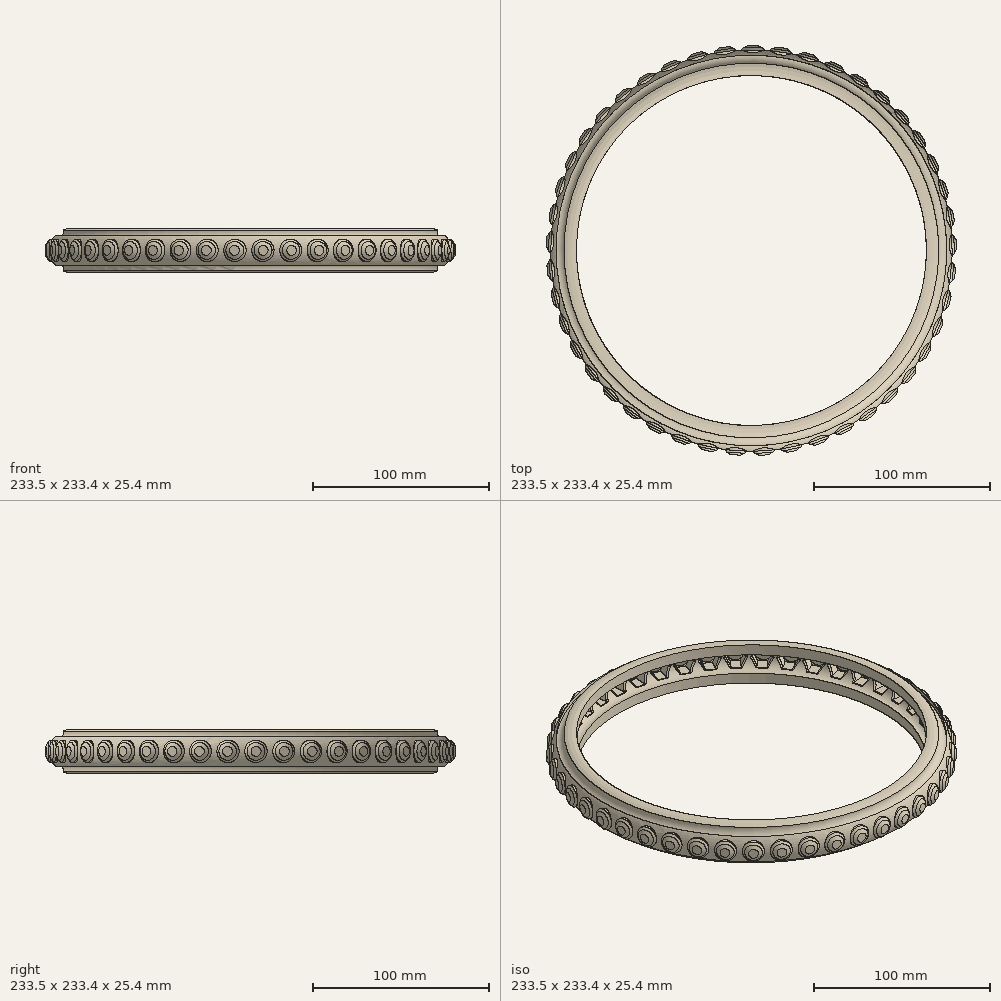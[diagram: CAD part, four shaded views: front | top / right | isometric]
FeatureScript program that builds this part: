
annotation { "Feature Type Name" : "Feature", "Feature Type Description" : "" }
export const myFeature = defineFeature(function(context is Context, id is Id, definition is map)
    precondition{}
    {
        {
            var Q0;
            Q0=qCreatedBy(makeId("Right.planeOp"),FACE);
            var sketch = newSketch(context, id + "F0", { "sketchPlane" : qUnion([Q0])});
            skCircle(sketch, "E0", {"center": v(101.6, 0) * mm, "radius": 6.35 * mm});
            skSolve(sketch);
        }
        {
            var Q0;
            Q0=qCreatedBy(makeId("Right.planeOp"),FACE);
            var sketch = newSketch(context, id + "F1", { "sketchPlane" : qUnion([Q0])});
            skLineSegment(sketch, "E1", {"start": v(0, 25.2) * mm, "end": v(0, -19.53) * mm, "construction": true});
            skSolve(sketch);
        }
        {
            var Q0;
            Q0 = qSketchRegion(id + "F0", true);
            var Q1;
            Q1=sQuery(id+"F1.wireOp",EDGE,"E1");
            revolve(context, id + "F2", {"entities" : qUnion([Q0]), "axis" : qUnion([Q1]), "revolveType" : RevolveType.FULL});
        }
        {
            var Q0;
            Q0=qCreatedBy(makeId("Top.planeOp"),FACE);
            var sketch = newSketch(context, id + "F3", { "sketchPlane" : qUnion([Q0])});
            skCircle(sketch, "E2", {"center": v(0, 0) * mm, "radius": 99.66 * mm});
            skSolve(sketch);
        }
        {
            var Q0;
            Q0=makeQuery(id+"F3.imprint","IMPRINT",FACE,{"disambiguationData":[TD([[makeQuery(id+"F3.imprint","IMPRINT",EDGE,{"derivedFrom":sQuery(id+"F3.wireOp",EDGE,"E2")}),1.0]])]});
            extrude(context, id + "F4", {"entities" : qUnion([Q0]), "operationType" : NewBodyOperationType.REMOVE, "endBound" : BoundingType.THROUGH_ALL, "depth" : 25.4 * mm, "hasSecondDirection" : true, "secondDirectionBound" : SecondDirectionBoundingType.THROUGH_ALL, "secondDirectionOppositeDirection" : true, "secondDirectionDepth" : 25.4 * mm});
        }
        {
            var Q0;
            Q0=makeQuery(id+"F4.boolean.opBoolean","COPY",FACE,{"derivedFrom":makeQuery(id+"F4.opExtrude","SWEPT_FACE",FACE,{"disambiguationData":[OSD([sQuery(id+"F3.wireOp",EDGE,"E2")])]})});
            var Q1;
            Q1=makeQuery(id+"F2.opRevolve","SWEPT_BODY",BODY,{"disambiguationData":[OSD([sQuery(id+"F0.wireOp",EDGE,"E0")])]});
            shell(context, id + "F5", {"entities" : qUnion([Q0]), "parts" : qUnion([Q1]), "thickness" : 6.35 * mm, "oppositeDirection" : true});
        }
        {
            var Q0;
            Q0=qCreatedBy(makeId("Top.planeOp"),FACE);
            var sketch = newSketch(context, id + "F6", { "sketchPlane" : qUnion([Q0])});
            skLineSegment(sketch, "E3", {"start": v(0.83, 108.72) * mm, "end": v(0.83, 116.7) * mm});
            skLineSegment(sketch, "E4", {"start": v(0.83, 116.7) * mm, "end": v(3.65, 116.7) * mm});
            skLineSegment(sketch, "E5", {"start": v(3.65, 116.7) * mm, "end": v(5.97, 115.34) * mm});
            skLineSegment(sketch, "E6", {"start": v(5.97, 113.6) * mm, "end": v(0.83, 108.72) * mm});
            skLineSegment(sketch, "E7", {"start": v(0.83, 94.91) * mm, "end": v(0.83, 120) * mm, "construction": true});
            skLineSegment(sketch, "E8", {"start": v(5.97, 115.34) * mm, "end": v(5.97, 113.6) * mm});
            skSolve(sketch);
        }
        {
            var Q0;
            Q0 = qSketchRegion(id + "F6", true);
            var Q1;
            Q1=sQuery(id+"F6.wireOp",EDGE,"E7");
            revolve(context, id + "F7", {"entities" : qUnion([Q0]), "axis" : qUnion([Q1]), "revolveType" : RevolveType.FULL});
        }
        {
            var Q0;
            Q0=makeQuery(id+"F7.opRevolve","SWEPT_BODY",BODY,{"disambiguationData":[OSD([sQuery(id+"F6.wireOp",EDGE,"E3"),sQuery(id+"F6.wireOp",EDGE,"E4"),sQuery(id+"F6.wireOp",EDGE,"E5"),sQuery(id+"F6.wireOp",EDGE,"E6"),sQuery(id+"F6.wireOp",EDGE,"E8")])]});
            var Q1;
            Q1=sQuery(id+"F1.wireOp",EDGE,"E1");
            circularPattern(context, id + "F8", {"entities" : qUnion([Q0]), "axis" : qUnion([Q1]), "angle" : 360 * degree, "instanceCount" : 45, "equalSpace" : true});
        }
        {
            var Q0;
            Q0=makeQuery(id+"F7.opRevolve","SWEPT_FACE",FACE,{"disambiguationData":[OSD([sQuery(id+"F6.wireOp",EDGE,"E4")])]});
            var sketch = newSketch(context, id + "F9", { "sketchPlane" : qUnion([Q0])});
            skCircle(sketch, "E9", {"center": v(-0.83, 0) * mm, "radius": 5.08 * mm});
            skCircle(sketch, "E10.0", {"center": v(-0.83, 0) * mm, "radius": 6.35 * mm});
            skSolve(sketch);
        }
        {
            var Q0;
            Q0 = qSketchRegion(id + "F9", true);
            var Q1;
            Q1=makeQuery(id+"F2.opRevolve","SWEPT_BODY",BODY,{"disambiguationData":[OSD([sQuery(id+"F0.wireOp",EDGE,"E0")])]});
            extrude(context, id + "F10", {"entities" : qUnion([Q0]), "endBound" : BoundingType.UP_TO_BODY, "oppositeDirection" : true, "endBoundEntityBody" : qUnion([Q1]), "depth" : 25.4 * mm});
        }
        {
            var Q0;
            Q0=makeQuery(id+"F10.opExtrude","CAP_EDGE",EDGE,{"disambiguationData":[OSD([sQuery(id+"F9.wireOp",EDGE,"E10.0")])],"isStart":true});
            chamfer(context, id + "F11", {"entities" : qUnion([Q0]), "chamferType" : ChamferType.TWO_OFFSETS, "width1" : 2.54 * mm, "oppositeDirection" : false, "width2" : 2.54 * mm, "tangentPropagation" : true});
        }
        {
            var Q0;
            Q0=makeQuery(id+"F10.opExtrude","SWEPT_BODY",BODY,{"disambiguationData":[OSD([sQuery(id+"F9.wireOp",EDGE,"E9"),sQuery(id+"F9.wireOp",EDGE,"E10.0")])]});
            var Q1;
            Q1=sQuery(id+"F1.wireOp",EDGE,"E1");
            circularPattern(context, id + "F12", {"entities" : qUnion([Q0]), "axis" : qUnion([Q1]), "angle" : 360 * degree, "instanceCount" : 45, "equalSpace" : true});
        }
        {
            var Q0;
            Q0=qCreatedBy(makeId("Front.planeOp"),FACE);
            var sketch = newSketch(context, id + "F13", { "sketchPlane" : qUnion([Q0])});
            skCircle(sketch, "E11.cCircle", {"center": v(0.54, -0.38) * mm, "radius": 5.03 * mm, "construction": true});
            skLineSegment(sketch, "E11.0", {"start": v(-5.26, -0.34) * mm, "end": v(-2.32, 4.67) * mm});
            skLineSegment(sketch, "E11.1", {"start": v(-2.32, 4.67) * mm, "end": v(3.48, 4.62) * mm});
            skLineSegment(sketch, "E11.2", {"start": v(3.48, 4.62) * mm, "end": v(6.34, -0.43) * mm});
            skLineSegment(sketch, "E11.3", {"start": v(6.34, -0.43) * mm, "end": v(3.4, -5.43) * mm});
            skLineSegment(sketch, "E11.4", {"start": v(3.4, -5.43) * mm, "end": v(-2.4, -5.38) * mm});
            skLineSegment(sketch, "E11.5", {"start": v(-2.4, -5.38) * mm, "end": v(-5.26, -0.34) * mm});
            skPoint(sketch, "E11.0.midPoint", {"position": v(-3.8, 2.17) * mm});
            skSolve(sketch);
        }
        {
            var Q0;
            Q0=makeQuery(id+"F13.imprint","IMPRINT",FACE,{"disambiguationData":[TD([[makeQuery(id+"F13.imprint","IMPRINT",EDGE,{"derivedFrom":sQuery(id+"F13.wireOp",EDGE,"E11.0")}),-1.0]])]});
            extrude(context, id + "F14", {"entities" : qUnion([Q0]), "operationType" : NewBodyOperationType.REMOVE, "oppositeDirection" : true, "depth" : 114.3 * mm});
        }
        {
            var Q0;
            Q0=makeQuery(id+"F14.boolean.opBoolean","INTERSECT",EDGE,{"derivedFrom":[makeQuery(id+"F5.opShell","OFFSET_FACE",FACE,{"disambiguationData":[OSD([sQuery(id+"F0.wireOp",EDGE,"E0")])]}),makeQuery(id+"F14.opExtrude","SWEPT_FACE",FACE,{"disambiguationData":[OSD([sQuery(id+"F13.wireOp",EDGE,"E11.2")])]})]});
            var Q1;
            Q1=makeQuery(id+"F14.boolean.opBoolean","INTERSECT",EDGE,{"derivedFrom":[makeQuery(id+"F5.opShell","OFFSET_FACE",FACE,{"disambiguationData":[OSD([sQuery(id+"F0.wireOp",EDGE,"E0")])]}),makeQuery(id+"F14.opExtrude","SWEPT_FACE",FACE,{"disambiguationData":[OSD([sQuery(id+"F13.wireOp",EDGE,"E11.0")])]})]});
            var Q2;
            Q2=makeQuery(id+"F14.boolean.opBoolean","INTERSECT",EDGE,{"derivedFrom":[makeQuery(id+"F5.opShell","OFFSET_FACE",FACE,{"disambiguationData":[OSD([sQuery(id+"F0.wireOp",EDGE,"E0")])]}),makeQuery(id+"F14.opExtrude","SWEPT_FACE",FACE,{"disambiguationData":[OSD([sQuery(id+"F13.wireOp",EDGE,"E11.5")])]})]});
            var Q3;
            Q3=makeQuery(id+"F14.boolean.opBoolean","INTERSECT",EDGE,{"derivedFrom":[makeQuery(id+"F5.opShell","OFFSET_FACE",FACE,{"disambiguationData":[OSD([sQuery(id+"F0.wireOp",EDGE,"E0")])]}),makeQuery(id+"F14.opExtrude","SWEPT_FACE",FACE,{"disambiguationData":[OSD([sQuery(id+"F13.wireOp",EDGE,"E11.3")])]})]});
            var Q4;
            Q4=makeQuery(id+"F14.boolean.opBoolean","INTERSECT",EDGE,{"derivedFrom":[makeQuery(id+"F5.opShell","OFFSET_FACE",FACE,{"disambiguationData":[OSD([sQuery(id+"F0.wireOp",EDGE,"E0")])]}),makeQuery(id+"F14.opExtrude","SWEPT_FACE",FACE,{"disambiguationData":[OSD([sQuery(id+"F13.wireOp",EDGE,"E11.1")])]})]});
            var Q5;
            Q5=makeQuery(id+"F14.boolean.opBoolean","INTERSECT",EDGE,{"derivedFrom":[makeQuery(id+"F5.opShell","OFFSET_FACE",FACE,{"disambiguationData":[OSD([sQuery(id+"F0.wireOp",EDGE,"E0")])]}),makeQuery(id+"F14.opExtrude","SWEPT_FACE",FACE,{"disambiguationData":[OSD([sQuery(id+"F13.wireOp",EDGE,"E11.4")])]})]});
            chamfer(context, id + "F15", {"entities" : qUnion([Q0, Q1, Q2, Q3, Q4, Q5]), "width" : 1.02 * mm, "tangentPropagation" : true});
        }
        {
            var Q0;
            {var subQ0=sQuery(id+"F0.wireOp",EDGE,"E0");Q0=makeQuery(id+"F14.boolean.opBoolean","COPY",FACE,{"disambiguationData":[TD([makeQuery(id+"F2.opRevolve","SWEPT_FACE",FACE,{"disambiguationData":[OSD([subQ0])]}),makeQuery(id+"F5.opShell","OFFSET_FACE",FACE,{"disambiguationData":[OSD([subQ0])]}),makeQuery(id+"F14.opExtrude","SWEPT_FACE",FACE,{"disambiguationData":[OSD([sQuery(id+"F13.wireOp",EDGE,"E11.0")])]}),makeQuery(id+"F14.opExtrude","SWEPT_FACE",FACE,{"disambiguationData":[OSD([sQuery(id+"F13.wireOp",EDGE,"E11.2")])]})])],"derivedFrom":makeQuery(id+"F14.opExtrude","SWEPT_FACE",FACE,{"disambiguationData":[OSD([sQuery(id+"F13.wireOp",EDGE,"E11.1")])]})});}
            var Q1;
            Q1=makeQuery(id+"F15.opChamfer","BLEND_FACE",FACE,{"disambiguationData":[OSD([sQuery(id+"F0.wireOp",EDGE,"E0"),sQuery(id+"F13.wireOp",EDGE,"E11.1")])]});
            var Q2;
            {var subQ0=sQuery(id+"F0.wireOp",EDGE,"E0");Q2=makeQuery(id+"F14.boolean.opBoolean","COPY",FACE,{"disambiguationData":[TD([makeQuery(id+"F2.opRevolve","SWEPT_FACE",FACE,{"disambiguationData":[OSD([subQ0])]}),makeQuery(id+"F5.opShell","OFFSET_FACE",FACE,{"disambiguationData":[OSD([subQ0])]}),makeQuery(id+"F14.opExtrude","SWEPT_FACE",FACE,{"disambiguationData":[OSD([sQuery(id+"F13.wireOp",EDGE,"E11.1")])]}),makeQuery(id+"F14.opExtrude","SWEPT_FACE",FACE,{"disambiguationData":[OSD([sQuery(id+"F13.wireOp",EDGE,"E11.3")])]})])],"derivedFrom":makeQuery(id+"F14.opExtrude","SWEPT_FACE",FACE,{"disambiguationData":[OSD([sQuery(id+"F13.wireOp",EDGE,"E11.2")])]})});}
            var Q3;
            Q3=makeQuery(id+"F15.opChamfer","BLEND_FACE",FACE,{"disambiguationData":[OSD([sQuery(id+"F0.wireOp",EDGE,"E0"),sQuery(id+"F13.wireOp",EDGE,"E11.2")])]});
            var Q4;
            {var subQ0=sQuery(id+"F0.wireOp",EDGE,"E0");Q4=makeQuery(id+"F14.boolean.opBoolean","COPY",FACE,{"disambiguationData":[TD([makeQuery(id+"F2.opRevolve","SWEPT_FACE",FACE,{"disambiguationData":[OSD([subQ0])]})])],"derivedFrom":makeQuery(id+"F14.opExtrude","SWEPT_FACE",FACE,{"disambiguationData":[OSD([sQuery(id+"F13.wireOp",EDGE,"E11.0")])]})});}
            var Q5;
            Q5=makeQuery(id+"F15.opChamfer","BLEND_FACE",FACE,{"disambiguationData":[OSD([sQuery(id+"F0.wireOp",EDGE,"E0"),sQuery(id+"F13.wireOp",EDGE,"E11.0")])]});
            var Q6;
            {var subQ0=sQuery(id+"F0.wireOp",EDGE,"E0");Q6=makeQuery(id+"F14.boolean.opBoolean","COPY",FACE,{"disambiguationData":[TD([makeQuery(id+"F2.opRevolve","SWEPT_FACE",FACE,{"disambiguationData":[OSD([subQ0])]})])],"derivedFrom":makeQuery(id+"F14.opExtrude","SWEPT_FACE",FACE,{"disambiguationData":[OSD([sQuery(id+"F13.wireOp",EDGE,"E11.5")])]})});}
            var Q7;
            Q7=makeQuery(id+"F15.opChamfer","BLEND_FACE",FACE,{"disambiguationData":[OSD([sQuery(id+"F0.wireOp",EDGE,"E0"),sQuery(id+"F13.wireOp",EDGE,"E11.5")])]});
            var Q8;
            {var subQ0=sQuery(id+"F0.wireOp",EDGE,"E0");Q8=makeQuery(id+"F14.boolean.opBoolean","COPY",FACE,{"disambiguationData":[TD([makeQuery(id+"F2.opRevolve","SWEPT_FACE",FACE,{"disambiguationData":[OSD([subQ0])]}),makeQuery(id+"F5.opShell","OFFSET_FACE",FACE,{"disambiguationData":[OSD([subQ0])]}),makeQuery(id+"F14.opExtrude","SWEPT_FACE",FACE,{"disambiguationData":[OSD([sQuery(id+"F13.wireOp",EDGE,"E11.2")])]}),makeQuery(id+"F14.opExtrude","SWEPT_FACE",FACE,{"disambiguationData":[OSD([sQuery(id+"F13.wireOp",EDGE,"E11.4")])]})])],"derivedFrom":makeQuery(id+"F14.opExtrude","SWEPT_FACE",FACE,{"disambiguationData":[OSD([sQuery(id+"F13.wireOp",EDGE,"E11.3")])]})});}
            var Q9;
            Q9=makeQuery(id+"F15.opChamfer","BLEND_FACE",FACE,{"disambiguationData":[OSD([sQuery(id+"F0.wireOp",EDGE,"E0"),sQuery(id+"F13.wireOp",EDGE,"E11.3")])]});
            var Q10;
            Q10=makeQuery(id+"F15.opChamfer","BLEND_FACE",FACE,{"disambiguationData":[OSD([sQuery(id+"F0.wireOp",EDGE,"E0"),sQuery(id+"F13.wireOp",EDGE,"E11.4")])]});
            var Q11;
            {var subQ0=sQuery(id+"F0.wireOp",EDGE,"E0");Q11=makeQuery(id+"F14.boolean.opBoolean","COPY",FACE,{"disambiguationData":[TD([makeQuery(id+"F2.opRevolve","SWEPT_FACE",FACE,{"disambiguationData":[OSD([subQ0])]})])],"derivedFrom":makeQuery(id+"F14.opExtrude","SWEPT_FACE",FACE,{"disambiguationData":[OSD([sQuery(id+"F13.wireOp",EDGE,"E11.4")])]})});}
            var Q12;
            Q12=sQuery(id+"F1.wireOp",EDGE,"E1");
            circularPattern(context, id + "F16", {"faces" : qUnion([Q0, Q1, Q2, Q3, Q4, Q5, Q6, Q7, Q8, Q9, Q10, Q11]), "axis" : qUnion([Q12]), "angle" : 360 * degree, "instanceCount" : 45, "equalSpace" : true, "patternType" : PatternType.FACE});
        }
        {
            var Q0;
            Q0=qCreatedBy(makeId("Front.planeOp"),FACE);
            var sketch = newSketch(context, id + "F17", { "sketchPlane" : qUnion([Q0])});
            skArc(sketch, "E12", {"start": v(111.22, 15.23) * mm, "mid": v(106.55, 10.56) * mm, "end": v(111.22, 5.89) * mm});
            skLineSegment(sketch, "E13", {"start": v(111.22, 15.23) * mm, "end": v(111.22, 5.89) * mm});
            skLineSegment(sketch, "E14", {"start": v(111.22, 6.8) * mm, "end": v(111.22, 15.14) * mm, "construction": true});
            skArc(sketch, "E15.MirrorCS", {"start": v(111.22, -15.23) * mm, "mid": v(106.55, -10.56) * mm, "end": v(111.22, -5.89) * mm});
            skLineSegment(sketch, "E16.MirrorCS", {"start": v(111.22, -15.23) * mm, "end": v(111.22, -5.89) * mm});
            skSolve(sketch);
        }
        {
            var Q0;
            Q0 = qSketchRegion(id + "F17", true);
            var Q1;
            Q1=sQuery(id+"F1.wireOp",EDGE,"E1");
            revolve(context, id + "F18", {"operationType" : NewBodyOperationType.REMOVE, "entities" : qUnion([Q0]), "axis" : qUnion([Q1]), "revolveType" : RevolveType.FULL, "oppositeDirection" : true});
        }
    });
